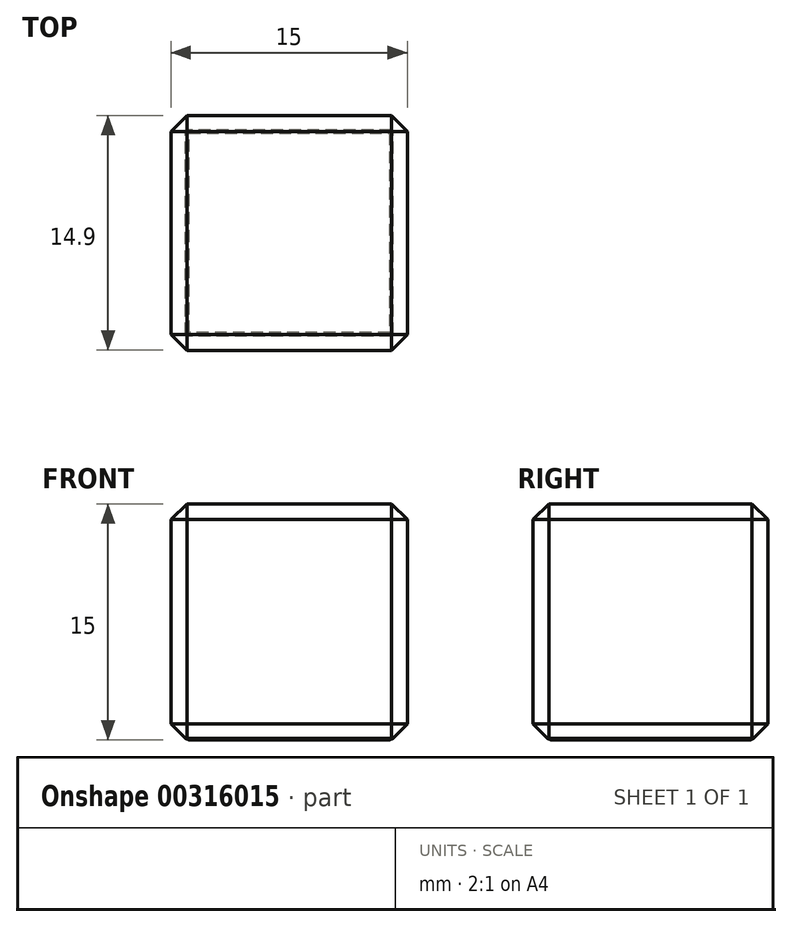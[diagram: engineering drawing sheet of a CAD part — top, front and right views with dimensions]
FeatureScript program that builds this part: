
annotation { "Feature Type Name" : "Feature", "Feature Type Description" : "" }
export const myFeature = defineFeature(function(context is Context, id is Id, definition is map)
    precondition{}
    {
        {
            var Q0;
            Q0=qCreatedBy(makeId("Top.planeOp"),FACE);
            var sketch = newSketch(context, id + "F0", { "sketchPlane" : qUnion([Q0])});
            skLineSegment(sketch, "E0.bottom", {"start": v(-7.5, 7.45) * mm, "end": v(7.5, 7.45) * mm});
            skLineSegment(sketch, "E0.top", {"start": v(-7.5, -7.45) * mm, "end": v(7.5, -7.45) * mm});
            skLineSegment(sketch, "E0.left", {"start": v(-7.5, 7.45) * mm, "end": v(-7.5, -7.45) * mm});
            skLineSegment(sketch, "E0.right", {"start": v(7.5, 7.45) * mm, "end": v(7.5, -7.45) * mm});
            skPoint(sketch, "E0.middle", {"position": v(0, 0) * mm});
            skSolve(sketch);
        }
        {
            var Q0;
            Q0=makeQuery(id+"F0.imprint","IMPRINT",FACE,{"disambiguationData":[TD([[makeQuery(id+"F0.imprint","IMPRINT",EDGE,{"derivedFrom":sQuery(id+"F0.wireOp",EDGE,"E0.bottom")}),-1.0]])]});
            extrude(context, id + "F1", {"entities" : qUnion([Q0]), "depth" : 15 * mm});
        }
        {
            var Q0;
            Q0=makeQuery(id+"F1.opExtrude","CAP_EDGE",EDGE,{"disambiguationData":[OSD([sQuery(id+"F0.wireOp",EDGE,"E0.bottom")])],"isStart":false});
            var Q1;
            Q1=makeQuery(id+"F1.opExtrude","CAP_EDGE",EDGE,{"disambiguationData":[OSD([sQuery(id+"F0.wireOp",EDGE,"E0.left")])],"isStart":false});
            var Q2;
            Q2=makeQuery(id+"F1.opExtrude","CAP_EDGE",EDGE,{"disambiguationData":[OSD([sQuery(id+"F0.wireOp",EDGE,"E0.right")])],"isStart":false});
            var Q3;
            Q3=makeQuery(id+"F1.opExtrude","CAP_EDGE",EDGE,{"disambiguationData":[OSD([sQuery(id+"F0.wireOp",EDGE,"E0.top")])],"isStart":false});
            var Q4;
            Q4=makeQuery(id+"F1.opExtrude","CAP_FACE",FACE,{"disambiguationData":[OSD([sQuery(id+"F0.wireOp",EDGE,"E0.bottom"),sQuery(id+"F0.wireOp",EDGE,"E0.top"),sQuery(id+"F0.wireOp",EDGE,"E0.left"),sQuery(id+"F0.wireOp",EDGE,"E0.right")])],"isStart":true});
            var Q5;
            Q5=makeQuery(id+"F1.opExtrude","SWEPT_EDGE",EDGE,{"disambiguationData":[OSD([sQuery(id+"F0.wireOp",EDGE,"E0.top"),sQuery(id+"F0.wireOp",EDGE,"E0.left")])]});
            var Q6;
            Q6=makeQuery(id+"F1.opExtrude","SWEPT_EDGE",EDGE,{"disambiguationData":[OSD([sQuery(id+"F0.wireOp",EDGE,"E0.bottom"),sQuery(id+"F0.wireOp",EDGE,"E0.left")])]});
            var Q7;
            Q7=makeQuery(id+"F1.opExtrude","SWEPT_EDGE",EDGE,{"disambiguationData":[OSD([sQuery(id+"F0.wireOp",EDGE,"E0.bottom"),sQuery(id+"F0.wireOp",EDGE,"E0.right")])]});
            var Q8;
            Q8=makeQuery(id+"F1.opExtrude","SWEPT_EDGE",EDGE,{"disambiguationData":[OSD([sQuery(id+"F0.wireOp",EDGE,"E0.top"),sQuery(id+"F0.wireOp",EDGE,"E0.right")])]});
            chamfer(context, id + "F2", {"entities" : qUnion([Q0, Q1, Q2, Q3, Q4, Q5, Q6, Q7, Q8]), "width" : 1 * mm, "tangentPropagation" : true});
        }
        {
            var Q0;
            Q0=makeQuery(id+"F1.opExtrude","CAP_FACE",FACE,{"disambiguationData":[OSD([sQuery(id+"F0.wireOp",EDGE,"E0.bottom"),sQuery(id+"F0.wireOp",EDGE,"E0.top"),sQuery(id+"F0.wireOp",EDGE,"E0.left"),sQuery(id+"F0.wireOp",EDGE,"E0.right")])],"isStart":true});
            chamfer(context, id + "F3", {"entities" : qUnion([Q0]), "width" : 0.3 * mm, "tangentPropagation" : true});
        }
    });
